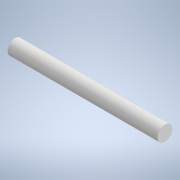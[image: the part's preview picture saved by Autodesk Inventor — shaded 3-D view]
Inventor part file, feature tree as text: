
AUTODESK INVENTOR PART (.ipt)
format: ipt  version: 2021 (Build 250183000, 183)  size: 131,072 bytes
history: native  units: mm
features: other x2, extrude x2, fillet x2, sketch x2, projected_geometry x1
ambient origin geometry x8: Origin, YZ Plane, XZ Plane, XY Plane, X Axis, Y Axis, Z Axis, Center Point
bodies: Body1 (feature_tree)
feature tree (9):
  other  "Bryła1"
  other  "Płaszczyzna konstrukcyjna1"
  extrude  "Wyciągnięcie proste1"  Depth=6.0mm
  extrude  "Wyciągnięcie proste2"  Depth=60.0mm TaperAngle=0.0deg
  fillet  "Zaokrąglenie1"  Radius=40.0mm
  fillet  "Zaokrąglenie2"  Radius=15.0mm
  sketch  "Szkic1"
  sketch  "Szkic2"
  projected_geometry  "Pętla rzutowana1"
